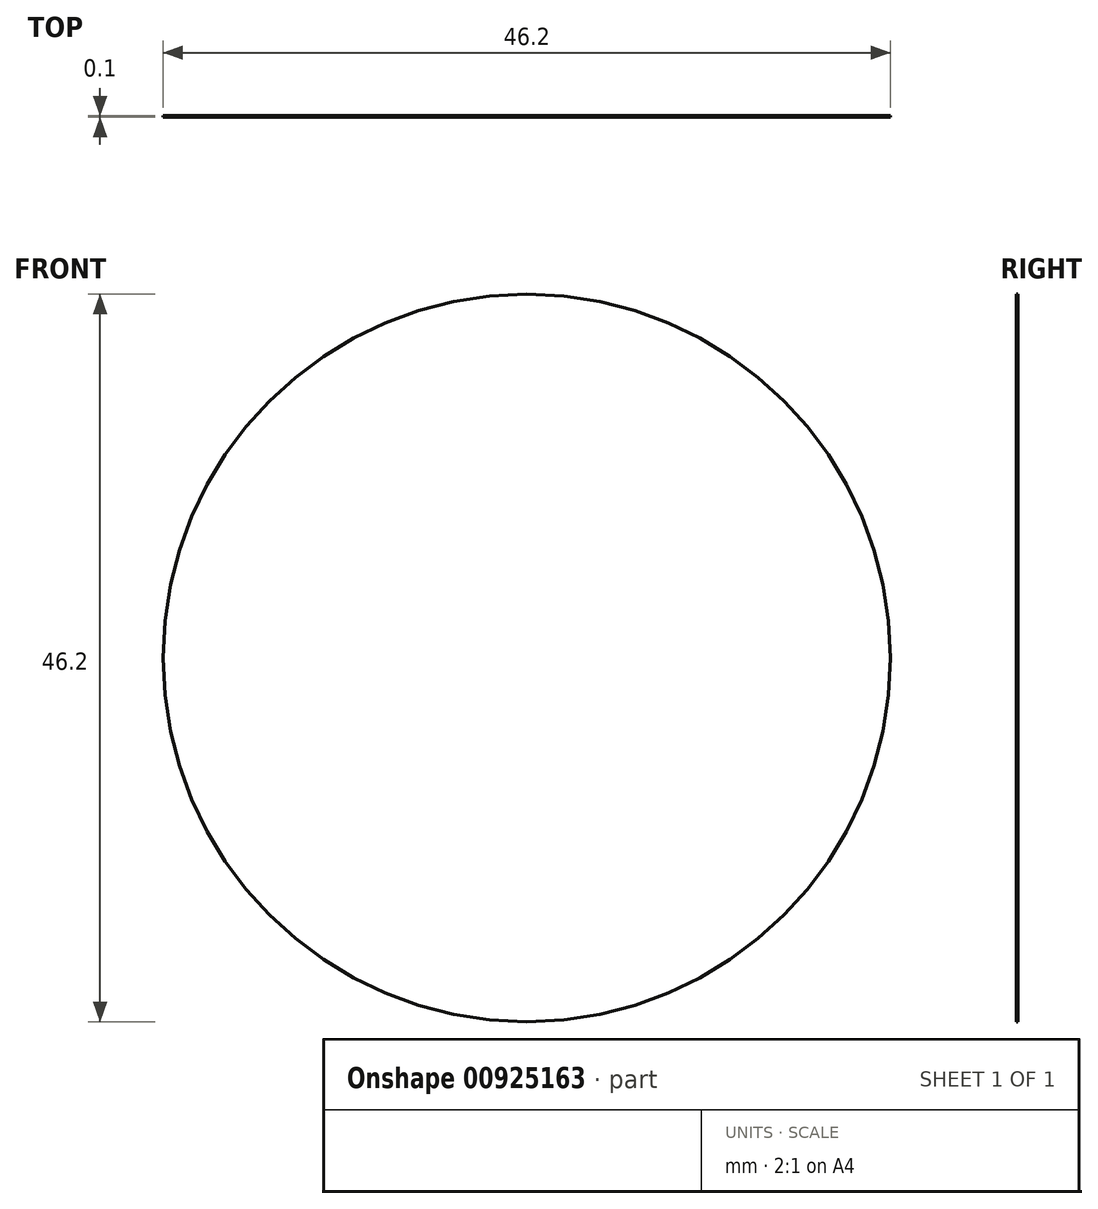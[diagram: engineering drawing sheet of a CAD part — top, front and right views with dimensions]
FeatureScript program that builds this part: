
annotation { "Feature Type Name" : "Feature", "Feature Type Description" : "" }
export const myFeature = defineFeature(function(context is Context, id is Id, definition is map)
    precondition{}
    {
        {
            var Q0;
            Q0=qCreatedBy(makeId("Front.planeOp"),FACE);
            var sketch = newSketch(context, id + "F0", { "sketchPlane" : qUnion([Q0])});
            skCircle(sketch, "E0", {"center": v(0, 0) * mm, "radius": 23.1 * mm});
            skSolve(sketch);
        }
        {
            var Q0;
            Q0 = qSketchRegion(id + "F0", true);
            extrude(context, id + "F1", {"entities" : qUnion([Q0]), "depth" : 0.1 * mm, "offsetDistance" : 25 * mm});
        }
    });
